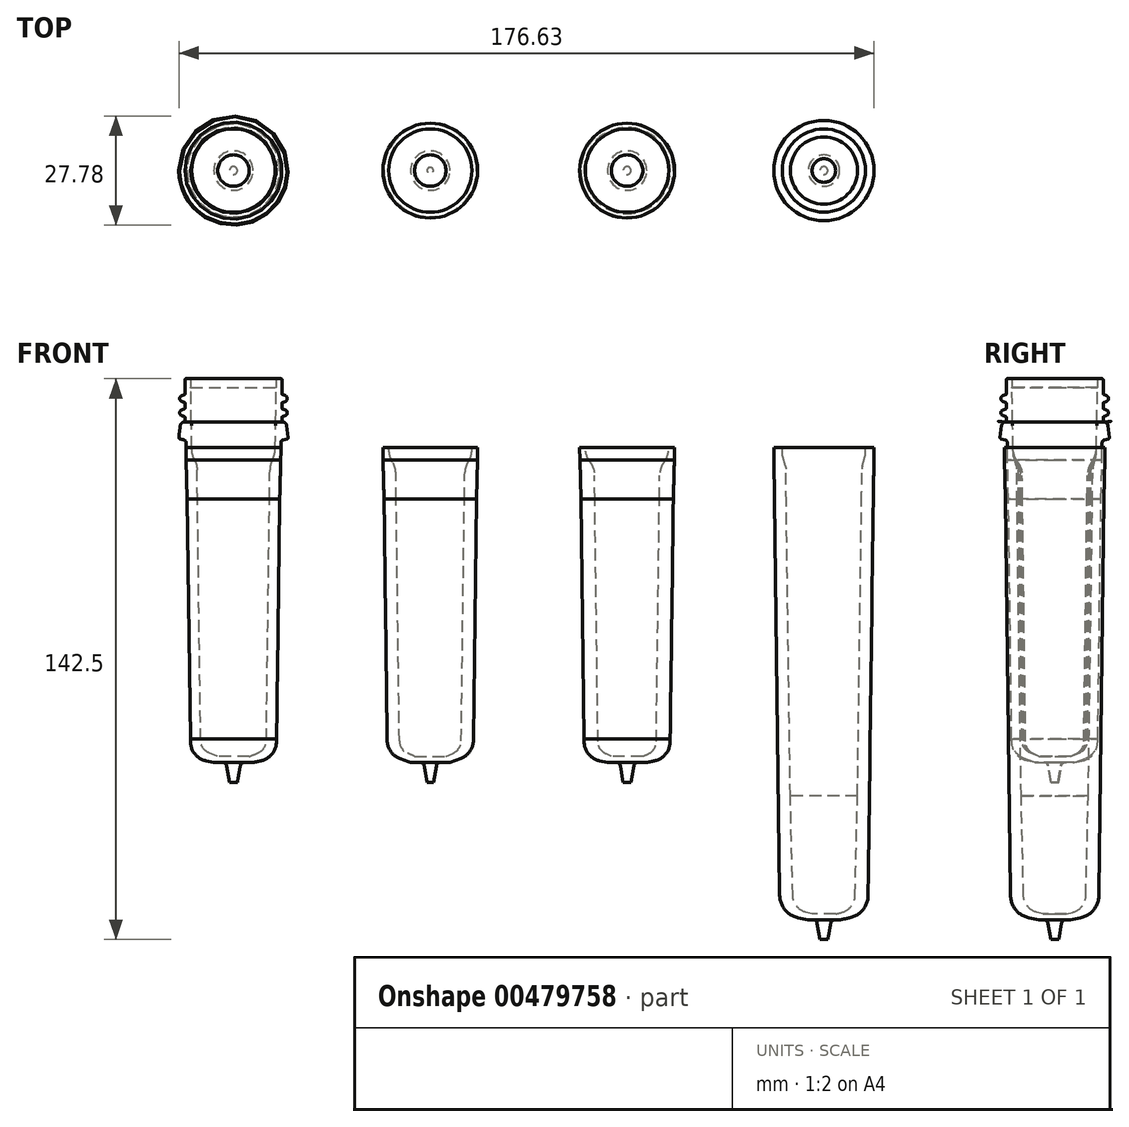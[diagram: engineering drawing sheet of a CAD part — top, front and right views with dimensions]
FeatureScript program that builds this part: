
annotation { "Feature Type Name" : "Feature", "Feature Type Description" : "" }
export const myFeature = defineFeature(function(context is Context, id is Id, definition is map)
    precondition{}
    {
        {
            var Q0;
            Q0=qCreatedBy(makeId("Front.planeOp"),FACE);
            var sketch = newSketch(context, id + "F0", { "sketchPlane" : qUnion([Q0])});
            skLineSegment(sketch, "E0", {"start": v(70.2, -70.1) * mm, "end": v(67.2, -70.1) * mm});
            skLineSegment(sketch, "E1", {"start": v(70.2, -70.1) * mm, "end": v(73.2, -70.1) * mm});
            skLineSegment(sketch, "E2", {"start": v(81.03, 63.6) * mm, "end": v(80.73, 46.79) * mm});
            skLineSegment(sketch, "E3", {"start": v(80.62, 46.02) * mm, "end": v(79.98, 43.78) * mm});
            skLineSegment(sketch, "E4", {"start": v(58.17, 65.9) * mm, "end": v(58.97, 65.9) * mm});
            skLineSegment(sketch, "E5", {"start": v(59.37, 65.5) * mm, "end": v(59.37, 63.6) * mm});
            skLineSegment(sketch, "E6", {"start": v(81.03, 65.5) * mm, "end": v(81.03, 63.6) * mm});
            skArc(sketch, "E7", {"start": v(59.37, 65.5) * mm, "mid": v(59.25, 65.78) * mm, "end": v(58.97, 65.9) * mm});
            skArc(sketch, "E8", {"start": v(81.43, 65.9) * mm, "mid": v(81.15, 65.78) * mm, "end": v(81.03, 65.5) * mm});
            skLineSegment(sketch, "E9", {"start": v(79.87, 43) * mm, "end": v(79.77, 34.4) * mm});
            skLineSegment(sketch, "E10", {"start": v(59.37, 63.6) * mm, "end": v(59.67, 46.79) * mm});
            skLineSegment(sketch, "E11", {"start": v(59.78, 46.02) * mm, "end": v(60.42, 43.78) * mm});
            skLineSegment(sketch, "E12", {"start": v(60.54, 43) * mm, "end": v(60.64, 34.4) * mm});
            skLineSegment(sketch, "E13", {"start": v(78.73, -40.1) * mm, "end": v(79.77, 34.4) * mm});
            skLineSegment(sketch, "E14", {"start": v(61.67, -40.1) * mm, "end": v(60.64, 34.4) * mm});
            skLineSegment(sketch, "E15", {"start": v(73.2, -70.1) * mm, "end": v(74.78, -69.68) * mm});
            skArc(sketch, "E16", {"start": v(74.78, -69.68) * mm, "mid": v(77.15, -68.12) * mm, "end": v(78.1, -65.44) * mm});
            skLineSegment(sketch, "E17", {"start": v(78.1, -65.44) * mm, "end": v(78.73, -40.1) * mm});
            skLineSegment(sketch, "E18", {"start": v(67.2, -70.1) * mm, "end": v(65.63, -69.68) * mm});
            skArc(sketch, "E19", {"start": v(62.3, -65.44) * mm, "mid": v(63.25, -68.12) * mm, "end": v(65.63, -69.68) * mm});
            skLineSegment(sketch, "E20", {"start": v(62.3, -65.44) * mm, "end": v(61.67, -40.1) * mm});
            skLineSegment(sketch, "E21", {"start": v(82.49, 60.98) * mm, "end": v(82.49, 65.65) * mm});
            skArc(sketch, "E22", {"start": v(57.07, 62.5) * mm, "mid": v(56.56, 61.78) * mm, "end": v(57.07, 61.05) * mm});
            skLineSegment(sketch, "E23", {"start": v(56.31, 51.1) * mm, "end": v(56.68, 54.02) * mm});
            skArc(sketch, "E24", {"start": v(56.31, 51.1) * mm, "mid": v(56.37, 50.86) * mm, "end": v(56.58, 50.72) * mm});
            skLineSegment(sketch, "E25", {"start": v(58.32, 49.75) * mm, "end": v(58.32, 48.4) * mm});
            skLineSegment(sketch, "E26", {"start": v(57.79, 50.43) * mm, "end": v(56.58, 50.72) * mm});
            skArc(sketch, "E27", {"start": v(58.32, 49.75) * mm, "mid": v(58.17, 50.18) * mm, "end": v(57.79, 50.43) * mm});
            skLineSegment(sketch, "E28", {"start": v(57.92, 55.1) * mm, "end": v(57.92, 57.14) * mm});
            skArc(sketch, "E29", {"start": v(57.72, 54.9) * mm, "mid": v(57.86, 54.96) * mm, "end": v(57.92, 55.1) * mm});
            skLineSegment(sketch, "E30", {"start": v(57.72, 54.9) * mm, "end": v(57.58, 54.9) * mm});
            skArc(sketch, "E31", {"start": v(57.58, 54.9) * mm, "mid": v(56.98, 54.62) * mm, "end": v(56.68, 54.02) * mm});
            skLineSegment(sketch, "E32", {"start": v(57.92, 60.74) * mm, "end": v(57.07, 61.05) * mm});
            skLineSegment(sketch, "E33", {"start": v(57.92, 57.14) * mm, "end": v(57.07, 57.45) * mm});
            skArc(sketch, "E34", {"start": v(57.07, 58.9) * mm, "mid": v(56.56, 58.18) * mm, "end": v(57.07, 57.45) * mm});
            skLineSegment(sketch, "E35", {"start": v(57.92, 59.2) * mm, "end": v(57.07, 58.9) * mm});
            skLineSegment(sketch, "E36", {"start": v(57.92, 59.2) * mm, "end": v(57.92, 60.74) * mm});
            skLineSegment(sketch, "E37", {"start": v(84.09, 51.1) * mm, "end": v(83.72, 54.02) * mm});
            skLineSegment(sketch, "E38", {"start": v(82.62, 50.43) * mm, "end": v(83.83, 50.72) * mm});
            skArc(sketch, "E39", {"start": v(83.83, 50.72) * mm, "mid": v(84.03, 50.86) * mm, "end": v(84.09, 51.1) * mm});
            skLineSegment(sketch, "E40", {"start": v(82.09, 49.75) * mm, "end": v(82.09, 48.4) * mm});
            skArc(sketch, "E41", {"start": v(82.62, 50.43) * mm, "mid": v(82.23, 50.18) * mm, "end": v(82.09, 49.75) * mm});
            skArc(sketch, "E42", {"start": v(83.33, 55.63) * mm, "mid": v(83.84, 56.35) * mm, "end": v(83.33, 57.08) * mm});
            skArc(sketch, "E43", {"start": v(83.72, 54.02) * mm, "mid": v(83.42, 54.62) * mm, "end": v(82.82, 54.9) * mm});
            skLineSegment(sketch, "E44", {"start": v(82.69, 54.9) * mm, "end": v(82.82, 54.9) * mm});
            skArc(sketch, "E45", {"start": v(82.49, 55.1) * mm, "mid": v(82.54, 54.96) * mm, "end": v(82.69, 54.9) * mm});
            skLineSegment(sketch, "E46", {"start": v(82.49, 55.1) * mm, "end": v(82.49, 55.32) * mm});
            skLineSegment(sketch, "E47", {"start": v(82.49, 55.32) * mm, "end": v(83.33, 55.63) * mm});
            skLineSegment(sketch, "E48", {"start": v(82.49, 60.98) * mm, "end": v(83.33, 60.68) * mm});
            skLineSegment(sketch, "E49", {"start": v(82.49, 57.38) * mm, "end": v(82.49, 58.92) * mm});
            skLineSegment(sketch, "E50", {"start": v(82.49, 57.38) * mm, "end": v(83.33, 57.08) * mm});
            skLineSegment(sketch, "E51", {"start": v(82.49, 58.92) * mm, "end": v(83.33, 59.23) * mm});
            skArc(sketch, "E52", {"start": v(83.33, 59.23) * mm, "mid": v(83.84, 59.95) * mm, "end": v(83.33, 60.68) * mm});
            skLineSegment(sketch, "E53", {"start": v(57.92, 62.8) * mm, "end": v(57.92, 65.65) * mm});
            skLineSegment(sketch, "E54", {"start": v(57.92, 62.8) * mm, "end": v(57.07, 62.5) * mm});
            skLineSegment(sketch, "E55", {"start": v(82.95, 48.4) * mm, "end": v(82.93, 45.4) * mm});
            skLineSegment(sketch, "E56", {"start": v(82.93, 45.4) * mm, "end": v(82.75, 35.4) * mm});
            skLineSegment(sketch, "E57", {"start": v(82.75, 35.4) * mm, "end": v(81.44, -64.6) * mm});
            skLineSegment(sketch, "E58", {"start": v(57.45, 48.4) * mm, "end": v(57.48, 45.4) * mm});
            skLineSegment(sketch, "E59", {"start": v(57.48, 45.4) * mm, "end": v(57.65, 35.4) * mm});
            skLineSegment(sketch, "E60", {"start": v(57.65, 35.4) * mm, "end": v(58.96, -64.6) * mm});
            skLineSegment(sketch, "E61", {"start": v(69.2, -76.6) * mm, "end": v(68.47, -72.43) * mm});
            skLineSegment(sketch, "E62", {"start": v(66.2, -71.6) * mm, "end": v(63.57, -71.04) * mm});
            skLineSegment(sketch, "E63", {"start": v(71.2, -76.6) * mm, "end": v(71.94, -72.43) * mm});
            skLineSegment(sketch, "E64", {"start": v(74.2, -71.6) * mm, "end": v(76.76, -71.06) * mm});
            skArc(sketch, "E65", {"start": v(76.76, -71.06) * mm, "mid": v(80.1, -69.03) * mm, "end": v(81.43, -65.37) * mm});
            skArc(sketch, "E66", {"start": v(72.92, -71.6) * mm, "mid": v(72.28, -71.84) * mm, "end": v(71.94, -72.43) * mm});
            skArc(sketch, "E67", {"start": v(68.47, -72.43) * mm, "mid": v(68.12, -71.84) * mm, "end": v(67.48, -71.6) * mm});
            skLineSegment(sketch, "E68", {"start": v(81.44, -64.6) * mm, "end": v(81.43, -65.37) * mm});
            skArc(sketch, "E69", {"start": v(58.97, -65.37) * mm, "mid": v(60.3, -69.03) * mm, "end": v(63.64, -71.06) * mm});
            skLineSegment(sketch, "E70", {"start": v(58.96, -64.6) * mm, "end": v(58.97, -65.37) * mm});
            skLineSegment(sketch, "E71", {"start": v(71.2, -76.6) * mm, "end": v(69.2, -76.6) * mm});
            skArc(sketch, "E72", {"start": v(59.67, 46.79) * mm, "mid": v(59.7, 46.4) * mm, "end": v(59.78, 46.02) * mm});
            skArc(sketch, "E73", {"start": v(60.54, 43) * mm, "mid": v(60.5, 43.4) * mm, "end": v(60.42, 43.78) * mm});
            skArc(sketch, "E74", {"start": v(80.62, 46.02) * mm, "mid": v(80.7, 46.4) * mm, "end": v(80.73, 46.79) * mm});
            skArc(sketch, "E75", {"start": v(79.98, 43.78) * mm, "mid": v(79.9, 43.4) * mm, "end": v(79.87, 43) * mm});
            skLineSegment(sketch, "E76", {"start": v(58.32, 48.4) * mm, "end": v(57.45, 48.4) * mm});
            skArc(sketch, "E77", {"start": v(58.17, 65.9) * mm, "mid": v(57.99, 65.82) * mm, "end": v(57.92, 65.65) * mm});
            skLineSegment(sketch, "E78", {"start": v(81.43, 65.9) * mm, "end": v(82.24, 65.9) * mm});
            skArc(sketch, "E79", {"start": v(82.49, 65.65) * mm, "mid": v(82.41, 65.82) * mm, "end": v(82.24, 65.9) * mm});
            skLineSegment(sketch, "E80", {"start": v(82.09, 48.4) * mm, "end": v(82.95, 48.4) * mm});
            skLineSegment(sketch, "E81", {"start": v(66.2, -71.6) * mm, "end": v(67.48, -71.6) * mm});
            skLineSegment(sketch, "E82", {"start": v(72.92, -71.6) * mm, "end": v(74.2, -71.6) * mm});
            skLineSegment(sketch, "E83", {"start": v(33.7, 54.02) * mm, "end": v(34.08, 51) * mm});
            skArc(sketch, "E84", {"start": v(33.82, 50.62) * mm, "mid": v(34.02, 50.76) * mm, "end": v(34.08, 51) * mm});
            skArc(sketch, "E85", {"start": v(32.78, 50.36) * mm, "mid": v(32.4, 50.12) * mm, "end": v(32.25, 49.68) * mm});
            skLineSegment(sketch, "E86", {"start": v(32.25, 48.4) * mm, "end": v(32.25, 49.68) * mm});
            skLineSegment(sketch, "E87", {"start": v(32.78, 50.36) * mm, "end": v(33.82, 50.62) * mm});
            skArc(sketch, "E88", {"start": v(33.36, 61.94) * mm, "mid": v(33.87, 62.66) * mm, "end": v(33.36, 63.39) * mm});
            skLineSegment(sketch, "E89", {"start": v(33.3, 54.71) * mm, "end": v(33.36, 54.74) * mm});
            skArc(sketch, "E90", {"start": v(33.7, 54.02) * mm, "mid": v(33.57, 54.41) * mm, "end": v(33.3, 54.71) * mm});
            skArc(sketch, "E91", {"start": v(33.36, 54.74) * mm, "mid": v(33.87, 55.46) * mm, "end": v(33.36, 56.19) * mm});
            skArc(sketch, "E92", {"start": v(33.36, 58.34) * mm, "mid": v(33.87, 59.06) * mm, "end": v(33.36, 59.79) * mm});
            skLineSegment(sketch, "E93", {"start": v(32.51, 57.89) * mm, "end": v(32.51, 56.64) * mm});
            skArc(sketch, "E94", {"start": v(32.51, 56.64) * mm, "mid": v(32.55, 56.52) * mm, "end": v(32.64, 56.45) * mm});
            skArc(sketch, "E95", {"start": v(32.64, 58.08) * mm, "mid": v(32.55, 58) * mm, "end": v(32.51, 57.89) * mm});
            skArc(sketch, "E96", {"start": v(32.51, 60.24) * mm, "mid": v(32.55, 60.12) * mm, "end": v(32.64, 60.05) * mm});
            skArc(sketch, "E97", {"start": v(32.64, 61.68) * mm, "mid": v(32.55, 61.6) * mm, "end": v(32.51, 61.49) * mm});
            skLineSegment(sketch, "E98", {"start": v(32.51, 61.49) * mm, "end": v(32.51, 60.24) * mm});
            skArc(sketch, "E99", {"start": v(32.51, 63.84) * mm, "mid": v(32.55, 63.72) * mm, "end": v(32.64, 63.65) * mm});
            skLineSegment(sketch, "E100", {"start": v(32.51, 65.65) * mm, "end": v(32.51, 63.84) * mm});
            skLineSegment(sketch, "E101", {"start": v(32.64, 56.45) * mm, "end": v(33.36, 56.19) * mm});
            skLineSegment(sketch, "E102", {"start": v(32.64, 58.08) * mm, "end": v(33.36, 58.34) * mm});
            skLineSegment(sketch, "E103", {"start": v(32.64, 60.05) * mm, "end": v(33.36, 59.79) * mm});
            skLineSegment(sketch, "E104", {"start": v(32.64, 61.68) * mm, "end": v(33.36, 61.94) * mm});
            skLineSegment(sketch, "E105", {"start": v(32.64, 63.65) * mm, "end": v(33.36, 63.39) * mm});
            skLineSegment(sketch, "E106", {"start": v(7.9, 65.65) * mm, "end": v(7.9, 62.9) * mm});
            skLineSegment(sketch, "E107", {"start": v(7.9, 62.9) * mm, "end": v(7.9, 62.04) * mm});
            skLineSegment(sketch, "E108", {"start": v(7.76, 61.85) * mm, "end": v(7.04, 61.59) * mm});
            skLineSegment(sketch, "E109", {"start": v(7.76, 59.88) * mm, "end": v(7.04, 60.14) * mm});
            skArc(sketch, "E110", {"start": v(7.04, 61.59) * mm, "mid": v(6.53, 60.86) * mm, "end": v(7.04, 60.14) * mm});
            skArc(sketch, "E111", {"start": v(7.76, 61.85) * mm, "mid": v(7.86, 61.92) * mm, "end": v(7.9, 62.04) * mm});
            skArc(sketch, "E112", {"start": v(7.9, 59.69) * mm, "mid": v(7.86, 59.8) * mm, "end": v(7.76, 59.88) * mm});
            skLineSegment(sketch, "E113", {"start": v(7.76, 58.25) * mm, "end": v(7.04, 57.99) * mm});
            skArc(sketch, "E114", {"start": v(7.76, 58.25) * mm, "mid": v(7.86, 58.32) * mm, "end": v(7.9, 58.44) * mm});
            skLineSegment(sketch, "E115", {"start": v(7.9, 59.69) * mm, "end": v(7.9, 58.44) * mm});
            skLineSegment(sketch, "E116", {"start": v(7.62, 50.36) * mm, "end": v(6.58, 50.62) * mm});
            skLineSegment(sketch, "E117", {"start": v(6.7, 54.02) * mm, "end": v(6.32, 51) * mm});
            skLineSegment(sketch, "E118", {"start": v(8.15, 48.4) * mm, "end": v(8.15, 49.68) * mm});
            skArc(sketch, "E119", {"start": v(8.15, 49.68) * mm, "mid": v(8, 50.12) * mm, "end": v(7.62, 50.36) * mm});
            skArc(sketch, "E120", {"start": v(6.32, 51) * mm, "mid": v(6.38, 50.76) * mm, "end": v(6.58, 50.62) * mm});
            skArc(sketch, "E121", {"start": v(7.7, 54.9) * mm, "mid": v(7.03, 54.65) * mm, "end": v(6.7, 54.02) * mm});
            skArc(sketch, "E122", {"start": v(7.7, 54.9) * mm, "mid": v(7.83, 54.95) * mm, "end": v(7.9, 55.1) * mm});
            skLineSegment(sketch, "E123", {"start": v(7.76, 56.28) * mm, "end": v(7.04, 56.54) * mm});
            skArc(sketch, "E124", {"start": v(7.04, 57.99) * mm, "mid": v(6.53, 57.26) * mm, "end": v(7.04, 56.54) * mm});
            skArc(sketch, "E125", {"start": v(7.9, 56.09) * mm, "mid": v(7.86, 56.2) * mm, "end": v(7.76, 56.28) * mm});
            skLineSegment(sketch, "E126", {"start": v(7.9, 56.09) * mm, "end": v(7.9, 55.1) * mm});
            skLineSegment(sketch, "E127", {"start": v(8.15, 48.4) * mm, "end": v(8.2, 45.3) * mm});
            skLineSegment(sketch, "E128", {"start": v(8.2, 45.3) * mm, "end": v(8.45, 35.3) * mm});
            skLineSegment(sketch, "E129", {"start": v(32.25, 48.4) * mm, "end": v(32.21, 45.3) * mm});
            skLineSegment(sketch, "E130", {"start": v(32.21, 45.3) * mm, "end": v(31.95, 35.3) * mm});
            skLineSegment(sketch, "E131", {"start": v(31.95, 35.3) * mm, "end": v(31.15, -25.6) * mm});
            skLineSegment(sketch, "E132", {"start": v(8.45, 35.3) * mm, "end": v(9.25, -25.6) * mm});
            skLineSegment(sketch, "E133", {"start": v(21.2, -36.6) * mm, "end": v(21.94, -32.43) * mm});
            skLineSegment(sketch, "E134", {"start": v(19.2, -36.6) * mm, "end": v(18.47, -32.43) * mm});
            skLineSegment(sketch, "E135", {"start": v(9.28, -25.6) * mm, "end": v(9.29, -26.36) * mm});
            skLineSegment(sketch, "E136", {"start": v(15.2, -31.6) * mm, "end": v(13.25, -31.19) * mm});
            skArc(sketch, "E137", {"start": v(9.29, -26.36) * mm, "mid": v(10.42, -29.47) * mm, "end": v(13.25, -31.19) * mm});
            skLineSegment(sketch, "E138", {"start": v(15.2, -31.6) * mm, "end": v(17.48, -31.6) * mm});
            skArc(sketch, "E139", {"start": v(18.47, -32.43) * mm, "mid": v(18.12, -31.84) * mm, "end": v(17.48, -31.6) * mm});
            skArc(sketch, "E140", {"start": v(22.92, -31.6) * mm, "mid": v(22.28, -31.84) * mm, "end": v(21.94, -32.43) * mm});
            skLineSegment(sketch, "E141", {"start": v(31.13, -25.6) * mm, "end": v(31.12, -26.36) * mm});
            skArc(sketch, "E142", {"start": v(27.16, -31.19) * mm, "mid": v(29.98, -29.47) * mm, "end": v(31.12, -26.36) * mm});
            skLineSegment(sketch, "E143", {"start": v(25.2, -31.6) * mm, "end": v(22.92, -31.6) * mm});
            skLineSegment(sketch, "E144", {"start": v(25.2, -31.6) * mm, "end": v(27.16, -31.19) * mm});
            skArc(sketch, "E145", {"start": v(12.8, -26.29) * mm, "mid": v(13.4, -28.2) * mm, "end": v(14.93, -29.46) * mm});
            skLineSegment(sketch, "E146", {"start": v(12, 35.3) * mm, "end": v(12.8, -26.29) * mm});
            skArc(sketch, "E147", {"start": v(9.35, 65.6) * mm, "mid": v(9.26, 65.8) * mm, "end": v(9.05, 65.9) * mm});
            skLineSegment(sketch, "E148", {"start": v(9.05, 65.9) * mm, "end": v(8.14, 65.9) * mm});
            skLineSegment(sketch, "E149", {"start": v(9.35, 65.6) * mm, "end": v(9.35, 63.62) * mm});
            skLineSegment(sketch, "E150", {"start": v(9.35, 63.6) * mm, "end": v(9.61, 48.24) * mm});
            skLineSegment(sketch, "E151", {"start": v(11.92, 41.34) * mm, "end": v(12, 35.3) * mm});
            skArc(sketch, "E152", {"start": v(25.47, -29.46) * mm, "mid": v(27.01, -28.2) * mm, "end": v(27.6, -26.29) * mm});
            skLineSegment(sketch, "E153", {"start": v(24.2, -30) * mm, "end": v(25.47, -29.46) * mm});
            skLineSegment(sketch, "E154", {"start": v(16.2, -30) * mm, "end": v(14.93, -29.46) * mm});
            skLineSegment(sketch, "E155", {"start": v(28.41, 35.3) * mm, "end": v(27.6, -26.29) * mm});
            skArc(sketch, "E156", {"start": v(31.36, 65.9) * mm, "mid": v(31.14, 65.8) * mm, "end": v(31.06, 65.6) * mm});
            skLineSegment(sketch, "E157", {"start": v(31.06, 65.6) * mm, "end": v(31.06, 63.6) * mm});
            skLineSegment(sketch, "E158", {"start": v(32.26, 65.9) * mm, "end": v(31.36, 65.9) * mm});
            skLineSegment(sketch, "E159", {"start": v(31.06, 63.6) * mm, "end": v(30.79, 48.24) * mm});
            skLineSegment(sketch, "E160", {"start": v(28.48, 41.34) * mm, "end": v(28.41, 35.3) * mm});
            skLineSegment(sketch, "E161", {"start": v(16.2, -30) * mm, "end": v(20.2, -30) * mm});
            skLineSegment(sketch, "E162", {"start": v(24.2, -30) * mm, "end": v(20.2, -30) * mm});
            skArc(sketch, "E163", {"start": v(11.92, 41.34) * mm, "mid": v(11.61, 43.16) * mm, "end": v(10.77, 44.8) * mm});
            skArc(sketch, "E164", {"start": v(9.61, 48.24) * mm, "mid": v(9.93, 46.43) * mm, "end": v(10.77, 44.8) * mm});
            skArc(sketch, "E165", {"start": v(29.64, 44.8) * mm, "mid": v(28.79, 43.16) * mm, "end": v(28.48, 41.34) * mm});
            skArc(sketch, "E166", {"start": v(29.64, 44.8) * mm, "mid": v(30.48, 46.43) * mm, "end": v(30.79, 48.24) * mm});
            skLineSegment(sketch, "E167", {"start": v(19.2, -36.6) * mm, "end": v(21.2, -36.6) * mm});
            skArc(sketch, "E168", {"start": v(8.14, 65.9) * mm, "mid": v(7.96, 65.82) * mm, "end": v(7.9, 65.65) * mm});
            skArc(sketch, "E169", {"start": v(32.51, 65.65) * mm, "mid": v(32.44, 65.82) * mm, "end": v(32.26, 65.9) * mm});
            skLineSegment(sketch, "E170", {"start": v(-41.85, 48.4) * mm, "end": v(-41.8, 45.3) * mm});
            skLineSegment(sketch, "E171", {"start": v(-41.8, 45.3) * mm, "end": v(-41.55, 35.3) * mm});
            skLineSegment(sketch, "E172", {"start": v(-17.75, 48.4) * mm, "end": v(-17.79, 45.3) * mm});
            skLineSegment(sketch, "E173", {"start": v(-17.79, 45.3) * mm, "end": v(-18.05, 35.3) * mm});
            skLineSegment(sketch, "E174", {"start": v(-18.05, 35.3) * mm, "end": v(-18.85, -25.6) * mm});
            skLineSegment(sketch, "E175", {"start": v(-41.55, 35.3) * mm, "end": v(-40.75, -25.6) * mm});
            skArc(sketch, "E176", {"start": v(-27.28, -31.6) * mm, "mid": v(-27.92, -31.84) * mm, "end": v(-28.26, -32.43) * mm});
            skLineSegment(sketch, "E177", {"start": v(-29, -36.6) * mm, "end": v(-28.26, -32.43) * mm});
            skLineSegment(sketch, "E178", {"start": v(-29, -36.6) * mm, "end": v(-29.8, -36.6) * mm});
            skLineSegment(sketch, "E179", {"start": v(-24.8, -31.6) * mm, "end": v(-21.93, -30.5) * mm});
            skLineSegment(sketch, "E180", {"start": v(-34.8, -31.6) * mm, "end": v(-37.66, -30.5) * mm});
            skLineSegment(sketch, "E181", {"start": v(-30.6, -36.6) * mm, "end": v(-29.8, -36.6) * mm});
            skLineSegment(sketch, "E182", {"start": v(-30.6, -36.6) * mm, "end": v(-31.33, -32.43) * mm});
            skArc(sketch, "E183", {"start": v(-31.33, -32.43) * mm, "mid": v(-31.68, -31.84) * mm, "end": v(-32.32, -31.6) * mm});
            skArc(sketch, "E184", {"start": v(-21.93, -30.5) * mm, "mid": v(-19.72, -28.77) * mm, "end": v(-18.85, -26.09) * mm});
            skArc(sketch, "E185", {"start": v(-40.74, -26.09) * mm, "mid": v(-39.88, -28.77) * mm, "end": v(-37.66, -30.5) * mm});
            skLineSegment(sketch, "E186", {"start": v(-18.85, -25.6) * mm, "end": v(-18.85, -26.09) * mm});
            skLineSegment(sketch, "E187", {"start": v(-40.75, -25.6) * mm, "end": v(-40.74, -26.09) * mm});
            skLineSegment(sketch, "E188", {"start": v(-33.8, -30) * mm, "end": v(-35.52, -29.27) * mm});
            skLineSegment(sketch, "E189", {"start": v(-38.46, 35.3) * mm, "end": v(-37.65, -26.1) * mm});
            skLineSegment(sketch, "E190", {"start": v(-40.65, 63.6) * mm, "end": v(-40.38, 47.9) * mm});
            skLineSegment(sketch, "E191", {"start": v(-40.65, 65.6) * mm, "end": v(-40.65, 63.62) * mm});
            skLineSegment(sketch, "E192", {"start": v(-40.95, 65.9) * mm, "end": v(-41.86, 65.9) * mm});
            skArc(sketch, "E193", {"start": v(-40.65, 65.6) * mm, "mid": v(-40.74, 65.8) * mm, "end": v(-40.95, 65.9) * mm});
            skLineSegment(sketch, "E194", {"start": v(-39.53, 44.92) * mm, "end": v(-39.39, 44.69) * mm});
            skLineSegment(sketch, "E195", {"start": v(-38.53, 41.67) * mm, "end": v(-38.46, 35.3) * mm});
            skArc(sketch, "E196", {"start": v(-37.65, -26.1) * mm, "mid": v(-37.06, -28) * mm, "end": v(-35.52, -29.27) * mm});
            skLineSegment(sketch, "E197", {"start": v(-21.14, 35.3) * mm, "end": v(-21.94, -26.1) * mm});
            skLineSegment(sketch, "E198", {"start": v(-18.94, 63.6) * mm, "end": v(-19.22, 47.9) * mm});
            skLineSegment(sketch, "E199", {"start": v(-18.94, 65.6) * mm, "end": v(-18.94, 63.6) * mm});
            skLineSegment(sketch, "E200", {"start": v(-17.74, 65.9) * mm, "end": v(-18.64, 65.9) * mm});
            skArc(sketch, "E201", {"start": v(-18.64, 65.9) * mm, "mid": v(-18.86, 65.8) * mm, "end": v(-18.94, 65.6) * mm});
            skLineSegment(sketch, "E202", {"start": v(-20.07, 44.92) * mm, "end": v(-20.2, 44.69) * mm});
            skLineSegment(sketch, "E203", {"start": v(-21.06, 41.67) * mm, "end": v(-21.14, 35.3) * mm});
            skLineSegment(sketch, "E204", {"start": v(-33.8, -30) * mm, "end": v(-29.8, -30) * mm});
            skLineSegment(sketch, "E205", {"start": v(-25.8, -30) * mm, "end": v(-24.08, -29.27) * mm});
            skArc(sketch, "E206", {"start": v(-24.08, -29.27) * mm, "mid": v(-22.54, -28) * mm, "end": v(-21.94, -26.1) * mm});
            skLineSegment(sketch, "E207", {"start": v(-25.8, -30) * mm, "end": v(-29.8, -30) * mm});
            skLineSegment(sketch, "E208", {"start": v(-16.3, 54.02) * mm, "end": v(-15.92, 51) * mm});
            skArc(sketch, "E209", {"start": v(-16.18, 50.62) * mm, "mid": v(-15.98, 50.76) * mm, "end": v(-15.92, 51) * mm});
            skArc(sketch, "E210", {"start": v(-17.22, 50.36) * mm, "mid": v(-17.6, 50.12) * mm, "end": v(-17.75, 49.68) * mm});
            skLineSegment(sketch, "E211", {"start": v(-17.75, 48.4) * mm, "end": v(-17.75, 49.68) * mm});
            skLineSegment(sketch, "E212", {"start": v(-17.22, 50.36) * mm, "end": v(-16.18, 50.62) * mm});
            skArc(sketch, "E213", {"start": v(-16.64, 61.94) * mm, "mid": v(-16.13, 62.66) * mm, "end": v(-16.64, 63.39) * mm});
            skLineSegment(sketch, "E214", {"start": v(-16.7, 54.71) * mm, "end": v(-16.64, 54.74) * mm});
            skArc(sketch, "E215", {"start": v(-16.3, 54.02) * mm, "mid": v(-16.43, 54.41) * mm, "end": v(-16.7, 54.71) * mm});
            skArc(sketch, "E216", {"start": v(-16.64, 54.74) * mm, "mid": v(-16.13, 55.46) * mm, "end": v(-16.64, 56.19) * mm});
            skArc(sketch, "E217", {"start": v(-16.64, 58.34) * mm, "mid": v(-16.13, 59.06) * mm, "end": v(-16.64, 59.79) * mm});
            skLineSegment(sketch, "E218", {"start": v(-17.49, 57.89) * mm, "end": v(-17.49, 56.64) * mm});
            skArc(sketch, "E219", {"start": v(-17.49, 56.64) * mm, "mid": v(-17.45, 56.52) * mm, "end": v(-17.36, 56.45) * mm});
            skArc(sketch, "E220", {"start": v(-17.36, 58.08) * mm, "mid": v(-17.45, 58) * mm, "end": v(-17.49, 57.89) * mm});
            skArc(sketch, "E221", {"start": v(-17.49, 60.24) * mm, "mid": v(-17.45, 60.12) * mm, "end": v(-17.36, 60.05) * mm});
            skArc(sketch, "E222", {"start": v(-17.36, 61.68) * mm, "mid": v(-17.45, 61.6) * mm, "end": v(-17.49, 61.49) * mm});
            skLineSegment(sketch, "E223", {"start": v(-17.49, 61.49) * mm, "end": v(-17.49, 60.24) * mm});
            skArc(sketch, "E224", {"start": v(-17.49, 63.84) * mm, "mid": v(-17.45, 63.72) * mm, "end": v(-17.36, 63.65) * mm});
            skLineSegment(sketch, "E225", {"start": v(-17.49, 65.65) * mm, "end": v(-17.49, 63.84) * mm});
            skLineSegment(sketch, "E226", {"start": v(-17.36, 56.45) * mm, "end": v(-16.64, 56.19) * mm});
            skLineSegment(sketch, "E227", {"start": v(-17.36, 58.08) * mm, "end": v(-16.64, 58.34) * mm});
            skLineSegment(sketch, "E228", {"start": v(-17.36, 60.05) * mm, "end": v(-16.64, 59.79) * mm});
            skLineSegment(sketch, "E229", {"start": v(-17.36, 61.68) * mm, "end": v(-16.64, 61.94) * mm});
            skLineSegment(sketch, "E230", {"start": v(-17.36, 63.65) * mm, "end": v(-16.64, 63.39) * mm});
            skLineSegment(sketch, "E231", {"start": v(-42.1, 65.65) * mm, "end": v(-42.1, 62.9) * mm});
            skLineSegment(sketch, "E232", {"start": v(-42.1, 62.9) * mm, "end": v(-42.1, 62.04) * mm});
            skLineSegment(sketch, "E233", {"start": v(-42.24, 61.85) * mm, "end": v(-42.96, 61.59) * mm});
            skLineSegment(sketch, "E234", {"start": v(-42.24, 59.88) * mm, "end": v(-42.96, 60.14) * mm});
            skArc(sketch, "E235", {"start": v(-42.96, 61.59) * mm, "mid": v(-43.47, 60.86) * mm, "end": v(-42.96, 60.14) * mm});
            skArc(sketch, "E236", {"start": v(-42.24, 61.85) * mm, "mid": v(-42.14, 61.92) * mm, "end": v(-42.1, 62.04) * mm});
            skArc(sketch, "E237", {"start": v(-42.1, 59.69) * mm, "mid": v(-42.14, 59.8) * mm, "end": v(-42.24, 59.88) * mm});
            skLineSegment(sketch, "E238", {"start": v(-42.24, 58.25) * mm, "end": v(-42.96, 57.99) * mm});
            skArc(sketch, "E239", {"start": v(-42.24, 58.25) * mm, "mid": v(-42.14, 58.32) * mm, "end": v(-42.1, 58.44) * mm});
            skLineSegment(sketch, "E240", {"start": v(-42.1, 59.69) * mm, "end": v(-42.1, 58.44) * mm});
            skLineSegment(sketch, "E241", {"start": v(-42.38, 50.36) * mm, "end": v(-43.42, 50.62) * mm});
            skLineSegment(sketch, "E242", {"start": v(-43.3, 54.02) * mm, "end": v(-43.68, 51) * mm});
            skLineSegment(sketch, "E243", {"start": v(-41.85, 48.4) * mm, "end": v(-41.85, 49.68) * mm});
            skArc(sketch, "E244", {"start": v(-41.85, 49.68) * mm, "mid": v(-42, 50.12) * mm, "end": v(-42.38, 50.36) * mm});
            skArc(sketch, "E245", {"start": v(-43.68, 51) * mm, "mid": v(-43.62, 50.76) * mm, "end": v(-43.42, 50.62) * mm});
            skArc(sketch, "E246", {"start": v(-42.3, 54.9) * mm, "mid": v(-42.97, 54.65) * mm, "end": v(-43.3, 54.02) * mm});
            skArc(sketch, "E247", {"start": v(-42.3, 54.9) * mm, "mid": v(-42.17, 54.95) * mm, "end": v(-42.1, 55.1) * mm});
            skLineSegment(sketch, "E248", {"start": v(-42.24, 56.28) * mm, "end": v(-42.96, 56.54) * mm});
            skArc(sketch, "E249", {"start": v(-42.96, 57.99) * mm, "mid": v(-43.47, 57.26) * mm, "end": v(-42.96, 56.54) * mm});
            skArc(sketch, "E250", {"start": v(-42.1, 56.09) * mm, "mid": v(-42.14, 56.2) * mm, "end": v(-42.24, 56.28) * mm});
            skLineSegment(sketch, "E251", {"start": v(-42.1, 56.09) * mm, "end": v(-42.1, 55.1) * mm});
            skLineSegment(sketch, "E252", {"start": v(-34.8, -31.6) * mm, "end": v(-32.32, -31.6) * mm});
            skLineSegment(sketch, "E253", {"start": v(-27.28, -31.6) * mm, "end": v(-24.8, -31.6) * mm});
            skArc(sketch, "E254", {"start": v(-40.38, 47.9) * mm, "mid": v(-40.15, 46.35) * mm, "end": v(-39.53, 44.92) * mm});
            skArc(sketch, "E255", {"start": v(-38.53, 41.67) * mm, "mid": v(-38.76, 43.24) * mm, "end": v(-39.39, 44.69) * mm});
            skArc(sketch, "E256", {"start": v(-20.07, 44.92) * mm, "mid": v(-19.45, 46.35) * mm, "end": v(-19.22, 47.9) * mm});
            skArc(sketch, "E257", {"start": v(-20.2, 44.69) * mm, "mid": v(-20.84, 43.24) * mm, "end": v(-21.06, 41.67) * mm});
            skArc(sketch, "E258", {"start": v(-17.49, 65.65) * mm, "mid": v(-17.56, 65.82) * mm, "end": v(-17.74, 65.9) * mm});
            skArc(sketch, "E259", {"start": v(-41.86, 65.9) * mm, "mid": v(-42.04, 65.82) * mm, "end": v(-42.1, 65.65) * mm});
            skLineSegment(sketch, "E260", {"start": v(-66.3, 54.02) * mm, "end": v(-65.92, 51) * mm});
            skArc(sketch, "E261", {"start": v(-66.18, 50.62) * mm, "mid": v(-65.98, 50.76) * mm, "end": v(-65.92, 51) * mm});
            skArc(sketch, "E262", {"start": v(-67.22, 50.36) * mm, "mid": v(-67.6, 50.12) * mm, "end": v(-67.75, 49.68) * mm});
            skLineSegment(sketch, "E263", {"start": v(-67.75, 48.4) * mm, "end": v(-67.75, 49.68) * mm});
            skLineSegment(sketch, "E264", {"start": v(-67.22, 50.36) * mm, "end": v(-66.18, 50.62) * mm});
            skArc(sketch, "E265", {"start": v(-66.64, 61.94) * mm, "mid": v(-66.13, 62.66) * mm, "end": v(-66.64, 63.39) * mm});
            skLineSegment(sketch, "E266", {"start": v(-66.7, 54.71) * mm, "end": v(-66.64, 54.74) * mm});
            skArc(sketch, "E267", {"start": v(-66.3, 54.02) * mm, "mid": v(-66.43, 54.41) * mm, "end": v(-66.7, 54.71) * mm});
            skArc(sketch, "E268", {"start": v(-66.64, 54.74) * mm, "mid": v(-66.13, 55.46) * mm, "end": v(-66.64, 56.19) * mm});
            skArc(sketch, "E269", {"start": v(-66.64, 58.34) * mm, "mid": v(-66.13, 59.06) * mm, "end": v(-66.64, 59.79) * mm});
            skLineSegment(sketch, "E270", {"start": v(-67.49, 57.89) * mm, "end": v(-67.49, 56.64) * mm});
            skArc(sketch, "E271", {"start": v(-67.49, 56.64) * mm, "mid": v(-67.45, 56.52) * mm, "end": v(-67.36, 56.45) * mm});
            skArc(sketch, "E272", {"start": v(-67.36, 58.08) * mm, "mid": v(-67.45, 58) * mm, "end": v(-67.49, 57.89) * mm});
            skArc(sketch, "E273", {"start": v(-67.49, 60.24) * mm, "mid": v(-67.45, 60.12) * mm, "end": v(-67.36, 60.05) * mm});
            skArc(sketch, "E274", {"start": v(-67.36, 61.68) * mm, "mid": v(-67.45, 61.6) * mm, "end": v(-67.49, 61.49) * mm});
            skLineSegment(sketch, "E275", {"start": v(-67.49, 61.49) * mm, "end": v(-67.49, 60.24) * mm});
            skArc(sketch, "E276", {"start": v(-67.49, 63.84) * mm, "mid": v(-67.45, 63.72) * mm, "end": v(-67.36, 63.65) * mm});
            skLineSegment(sketch, "E277", {"start": v(-67.49, 65.65) * mm, "end": v(-67.49, 63.84) * mm});
            skLineSegment(sketch, "E278", {"start": v(-67.36, 56.45) * mm, "end": v(-66.64, 56.19) * mm});
            skLineSegment(sketch, "E279", {"start": v(-67.36, 58.08) * mm, "end": v(-66.64, 58.34) * mm});
            skLineSegment(sketch, "E280", {"start": v(-67.36, 60.05) * mm, "end": v(-66.64, 59.79) * mm});
            skLineSegment(sketch, "E281", {"start": v(-67.36, 61.68) * mm, "end": v(-66.64, 61.94) * mm});
            skLineSegment(sketch, "E282", {"start": v(-67.36, 63.65) * mm, "end": v(-66.64, 63.39) * mm});
            skLineSegment(sketch, "E283", {"start": v(-92.1, 65.65) * mm, "end": v(-92.1, 62.9) * mm});
            skLineSegment(sketch, "E284", {"start": v(-92.1, 62.9) * mm, "end": v(-92.1, 62.04) * mm});
            skLineSegment(sketch, "E285", {"start": v(-92.24, 61.85) * mm, "end": v(-92.96, 61.59) * mm});
            skLineSegment(sketch, "E286", {"start": v(-92.24, 59.88) * mm, "end": v(-92.96, 60.14) * mm});
            skArc(sketch, "E287", {"start": v(-92.96, 61.59) * mm, "mid": v(-93.47, 60.86) * mm, "end": v(-92.96, 60.14) * mm});
            skArc(sketch, "E288", {"start": v(-92.24, 61.85) * mm, "mid": v(-92.14, 61.92) * mm, "end": v(-92.1, 62.04) * mm});
            skArc(sketch, "E289", {"start": v(-92.1, 59.69) * mm, "mid": v(-92.14, 59.8) * mm, "end": v(-92.24, 59.88) * mm});
            skLineSegment(sketch, "E290", {"start": v(-92.24, 58.25) * mm, "end": v(-92.96, 57.99) * mm});
            skArc(sketch, "E291", {"start": v(-92.24, 58.25) * mm, "mid": v(-92.14, 58.32) * mm, "end": v(-92.1, 58.44) * mm});
            skLineSegment(sketch, "E292", {"start": v(-92.1, 59.69) * mm, "end": v(-92.1, 58.44) * mm});
            skLineSegment(sketch, "E293", {"start": v(-92.38, 50.36) * mm, "end": v(-93.42, 50.62) * mm});
            skLineSegment(sketch, "E294", {"start": v(-93.3, 54.02) * mm, "end": v(-93.68, 51) * mm});
            skLineSegment(sketch, "E295", {"start": v(-91.85, 48.4) * mm, "end": v(-91.85, 49.68) * mm});
            skArc(sketch, "E296", {"start": v(-91.85, 49.68) * mm, "mid": v(-92, 50.12) * mm, "end": v(-92.38, 50.36) * mm});
            skArc(sketch, "E297", {"start": v(-93.68, 51) * mm, "mid": v(-93.62, 50.76) * mm, "end": v(-93.42, 50.62) * mm});
            skArc(sketch, "E298", {"start": v(-92.3, 54.9) * mm, "mid": v(-92.97, 54.65) * mm, "end": v(-93.3, 54.02) * mm});
            skArc(sketch, "E299", {"start": v(-92.3, 54.9) * mm, "mid": v(-92.17, 54.95) * mm, "end": v(-92.1, 55.1) * mm});
            skLineSegment(sketch, "E300", {"start": v(-92.24, 56.28) * mm, "end": v(-92.96, 56.54) * mm});
            skArc(sketch, "E301", {"start": v(-92.96, 57.99) * mm, "mid": v(-93.47, 57.26) * mm, "end": v(-92.96, 56.54) * mm});
            skArc(sketch, "E302", {"start": v(-92.1, 56.09) * mm, "mid": v(-92.14, 56.2) * mm, "end": v(-92.24, 56.28) * mm});
            skLineSegment(sketch, "E303", {"start": v(-92.1, 56.09) * mm, "end": v(-92.1, 55.1) * mm});
            skLineSegment(sketch, "E304", {"start": v(-91.85, 48.4) * mm, "end": v(-91.8, 45.3) * mm});
            skLineSegment(sketch, "E305", {"start": v(-91.8, 45.3) * mm, "end": v(-91.55, 35.3) * mm});
            skLineSegment(sketch, "E306", {"start": v(-67.75, 48.4) * mm, "end": v(-67.79, 45.3) * mm});
            skLineSegment(sketch, "E307", {"start": v(-67.79, 45.3) * mm, "end": v(-68.05, 35.3) * mm});
            skLineSegment(sketch, "E308", {"start": v(-68.05, 35.3) * mm, "end": v(-68.85, -25.6) * mm});
            skLineSegment(sketch, "E309", {"start": v(-91.55, 35.3) * mm, "end": v(-90.75, -25.6) * mm});
            skLineSegment(sketch, "E310", {"start": v(-78.8, -36.6) * mm, "end": v(-78.06, -32.43) * mm});
            skLineSegment(sketch, "E311", {"start": v(-80.8, -36.6) * mm, "end": v(-81.53, -32.43) * mm});
            skLineSegment(sketch, "E312", {"start": v(-90.72, -25.6) * mm, "end": v(-90.71, -26.36) * mm});
            skLineSegment(sketch, "E313", {"start": v(-84.8, -31.6) * mm, "end": v(-86.75, -31.19) * mm});
            skArc(sketch, "E314", {"start": v(-90.71, -26.36) * mm, "mid": v(-89.58, -29.47) * mm, "end": v(-86.75, -31.19) * mm});
            skLineSegment(sketch, "E315", {"start": v(-84.8, -31.6) * mm, "end": v(-82.52, -31.6) * mm});
            skArc(sketch, "E316", {"start": v(-81.53, -32.43) * mm, "mid": v(-81.88, -31.84) * mm, "end": v(-82.52, -31.6) * mm});
            skArc(sketch, "E317", {"start": v(-77.08, -31.6) * mm, "mid": v(-77.72, -31.84) * mm, "end": v(-78.06, -32.43) * mm});
            skLineSegment(sketch, "E318", {"start": v(-68.87, -25.6) * mm, "end": v(-68.88, -26.36) * mm});
            skArc(sketch, "E319", {"start": v(-72.84, -31.19) * mm, "mid": v(-70.02, -29.47) * mm, "end": v(-68.88, -26.36) * mm});
            skLineSegment(sketch, "E320", {"start": v(-74.8, -31.6) * mm, "end": v(-77.08, -31.6) * mm});
            skLineSegment(sketch, "E321", {"start": v(-74.8, -31.6) * mm, "end": v(-72.84, -31.19) * mm});
            skLineSegment(sketch, "E322", {"start": v(-70.65, 35.3) * mm, "end": v(-71.45, -26.01) * mm});
            skLineSegment(sketch, "E323", {"start": v(-88.95, 35.3) * mm, "end": v(-88.14, -25.99) * mm});
            skLineSegment(sketch, "E324", {"start": v(-90.65, 63.6) * mm, "end": v(-90.38, 48.02) * mm});
            skArc(sketch, "E325", {"start": v(-90.65, 65.6) * mm, "mid": v(-90.74, 65.8) * mm, "end": v(-90.95, 65.9) * mm});
            skLineSegment(sketch, "E326", {"start": v(-90.95, 65.9) * mm, "end": v(-91.86, 65.9) * mm});
            skLineSegment(sketch, "E327", {"start": v(-90.65, 65.6) * mm, "end": v(-90.65, 63.62) * mm});
            skLineSegment(sketch, "E328", {"start": v(-89.03, 42.66) * mm, "end": v(-88.95, 35.3) * mm});
            skLineSegment(sketch, "E329", {"start": v(-68.94, 63.6) * mm, "end": v(-69.21, 48.02) * mm});
            skArc(sketch, "E330", {"start": v(-68.64, 65.9) * mm, "mid": v(-68.85, 65.8) * mm, "end": v(-68.94, 65.6) * mm});
            skLineSegment(sketch, "E331", {"start": v(-68.94, 65.6) * mm, "end": v(-68.94, 63.6) * mm});
            skLineSegment(sketch, "E332", {"start": v(-67.74, 65.9) * mm, "end": v(-68.64, 65.9) * mm});
            skLineSegment(sketch, "E333", {"start": v(-70.56, 42.66) * mm, "end": v(-70.65, 35.3) * mm});
            skLineSegment(sketch, "E334", {"start": v(-83.8, -30.1) * mm, "end": v(-86.01, -29.16) * mm});
            skArc(sketch, "E335", {"start": v(-88.14, -25.99) * mm, "mid": v(-87.55, -27.9) * mm, "end": v(-86.01, -29.16) * mm});
            skLineSegment(sketch, "E336", {"start": v(-75.8, -30.1) * mm, "end": v(-73.58, -29.16) * mm});
            skLineSegment(sketch, "E337", {"start": v(-75.8, -30.1) * mm, "end": v(-79.8, -30.1) * mm});
            skLineSegment(sketch, "E338", {"start": v(-83.8, -30.1) * mm, "end": v(-79.8, -30.1) * mm});
            skArc(sketch, "E339", {"start": v(-73.58, -29.16) * mm, "mid": v(-72.05, -27.9) * mm, "end": v(-71.45, -25.99) * mm});
            skArc(sketch, "E340", {"start": v(-91.86, 65.9) * mm, "mid": v(-92.04, 65.82) * mm, "end": v(-92.1, 65.65) * mm});
            skArc(sketch, "E341", {"start": v(-67.49, 65.65) * mm, "mid": v(-67.56, 65.82) * mm, "end": v(-67.74, 65.9) * mm});
            skLineSegment(sketch, "E342", {"start": v(-80.8, -36.6) * mm, "end": v(-78.8, -36.6) * mm});
            skArc(sketch, "E343", {"start": v(-90.38, 48.02) * mm, "mid": v(-90.2, 46.65) * mm, "end": v(-89.7, 45.36) * mm});
            skArc(sketch, "E344", {"start": v(-89.03, 42.66) * mm, "mid": v(-89.21, 44.05) * mm, "end": v(-89.7, 45.36) * mm});
            skArc(sketch, "E345", {"start": v(-69.89, 45.36) * mm, "mid": v(-69.4, 46.65) * mm, "end": v(-69.21, 48.02) * mm});
            skArc(sketch, "E346", {"start": v(-69.89, 45.36) * mm, "mid": v(-70.38, 44.05) * mm, "end": v(-70.56, 42.66) * mm});
            skSolve(sketch);
        }
        {
            var Q0;
            Q0=qCreatedBy(makeId("Front.planeOp"),FACE);
            var sketch = newSketch(context, id + "F1", { "sketchPlane" : qUnion([Q0])});
            skLineSegment(sketch, "E347.0", {"start": v(-90.39, 48.42) * mm, "end": v(-90.38, 48.02) * mm});
            skArc(sketch, "E348.0", {"start": v(-90.38, 48.02) * mm, "mid": v(-90.2, 46.65) * mm, "end": v(-89.7, 45.36) * mm});
            skArc(sketch, "E349.0", {"start": v(-89.03, 42.66) * mm, "mid": v(-89.21, 44.05) * mm, "end": v(-89.7, 45.36) * mm});
            skLineSegment(sketch, "E350.0", {"start": v(-89.03, 42.66) * mm, "end": v(-88.95, 35.3) * mm});
            skLineSegment(sketch, "E351.0", {"start": v(-88.95, 35.3) * mm, "end": v(-88.14, -25.99) * mm});
            skLineSegment(sketch, "E352.0", {"start": v(-91.55, 35.3) * mm, "end": v(-90.75, -25.6) * mm});
            skLineSegment(sketch, "E353.0", {"start": v(-91.8, 45.3) * mm, "end": v(-91.55, 35.3) * mm});
            skLineSegment(sketch, "E354.0", {"start": v(-91.85, 48.4) * mm, "end": v(-91.8, 45.3) * mm});
            skLineSegment(sketch, "E355.0", {"start": v(-83.8, -30.1) * mm, "end": v(-79.8, -30.1) * mm});
            skLineSegment(sketch, "E356.0", {"start": v(-80.8, -36.6) * mm, "end": v(-81.53, -32.43) * mm});
            skArc(sketch, "E357.0", {"start": v(-81.53, -32.43) * mm, "mid": v(-81.88, -31.84) * mm, "end": v(-82.52, -31.6) * mm});
            skLineSegment(sketch, "E358.0", {"start": v(-84.8, -31.6) * mm, "end": v(-82.52, -31.6) * mm});
            skLineSegment(sketch, "E359.0", {"start": v(-83.8, -30.1) * mm, "end": v(-86.01, -29.16) * mm});
            skLineSegment(sketch, "E360.0", {"start": v(-84.8, -31.6) * mm, "end": v(-86.75, -31.19) * mm});
            skArc(sketch, "E361.0", {"start": v(-90.71, -26.36) * mm, "mid": v(-89.58, -29.47) * mm, "end": v(-86.75, -31.19) * mm});
            skArc(sketch, "E362.0", {"start": v(-88.14, -25.99) * mm, "mid": v(-87.55, -27.9) * mm, "end": v(-86.01, -29.16) * mm});
            skLineSegment(sketch, "E363.0", {"start": v(-90.72, -25.6) * mm, "end": v(-90.71, -26.36) * mm});
            skLineSegment(sketch, "E364", {"start": v(-90.72, -25.6) * mm, "end": v(-90.75, -25.6) * mm});
            skLineSegment(sketch, "E365", {"start": v(-79.8, -30.1) * mm, "end": v(-79.8, -36.6) * mm});
            skLineSegment(sketch, "E366.0", {"start": v(-80.8, -36.6) * mm, "end": v(-79.8, -36.6) * mm});
            skPoint(sketch, "E367.orphan", {"position": v(-78.8, -36.6) * mm});
            skLineSegment(sketch, "E368", {"start": v(-91.85, 48.4) * mm, "end": v(-90.39, 48.42) * mm});
            skSolve(sketch);
        }
        {
            var Q0;
            Q0=makeQuery(id+"F1.imprint","IMPRINT",FACE,{"disambiguationData":[TD([[makeQuery(id+"F1.imprint","IMPRINT",EDGE,{"derivedFrom":sQuery(id+"F1.wireOp",EDGE,"E347.0")}),-1.0]])]});
            var Q1;
            Q1=sQuery(id+"F1.wireOp",EDGE,"E365");
            revolve(context, id + "F2", {"entities" : qUnion([Q0]), "axis" : qUnion([Q1]), "revolveType" : RevolveType.FULL});
        }
        {
            var Q0;
            Q0=qCreatedBy(makeId("Front.planeOp"),FACE);
            var sketch = newSketch(context, id + "F3", { "sketchPlane" : qUnion([Q0])});
            skLineSegment(sketch, "E369.0", {"start": v(-90.65, 63.6) * mm, "end": v(-90.39, 48.4) * mm});
            skLineSegment(sketch, "E370.0", {"start": v(-91.85, 48.4) * mm, "end": v(-91.85, 49.68) * mm});
            skArc(sketch, "E371.0", {"start": v(-91.85, 49.68) * mm, "mid": v(-92, 50.12) * mm, "end": v(-92.38, 50.36) * mm});
            skLineSegment(sketch, "E372.0", {"start": v(-92.38, 50.36) * mm, "end": v(-93.42, 50.62) * mm});
            skArc(sketch, "E373.0", {"start": v(-93.68, 51) * mm, "mid": v(-93.62, 50.76) * mm, "end": v(-93.42, 50.62) * mm});
            skLineSegment(sketch, "E374.0", {"start": v(-93.3, 54.02) * mm, "end": v(-93.68, 51) * mm});
            skArc(sketch, "E375.0", {"start": v(-92.3, 54.9) * mm, "mid": v(-92.97, 54.65) * mm, "end": v(-93.3, 54.02) * mm});
            skArc(sketch, "E376.0", {"start": v(-92.3, 54.9) * mm, "mid": v(-92.17, 54.95) * mm, "end": v(-92.1, 55.1) * mm});
            skLineSegment(sketch, "E377.0", {"start": v(-92.1, 56.09) * mm, "end": v(-92.1, 55.1) * mm});
            skArc(sketch, "E378.0", {"start": v(-92.1, 56.09) * mm, "mid": v(-92.14, 56.2) * mm, "end": v(-92.24, 56.28) * mm});
            skLineSegment(sketch, "E379.0", {"start": v(-92.24, 56.28) * mm, "end": v(-92.96, 56.54) * mm});
            skArc(sketch, "E380.0", {"start": v(-92.96, 57.99) * mm, "mid": v(-93.47, 57.26) * mm, "end": v(-92.96, 56.54) * mm});
            skLineSegment(sketch, "E381.0", {"start": v(-92.24, 58.25) * mm, "end": v(-92.96, 57.99) * mm});
            skArc(sketch, "E382.0", {"start": v(-92.24, 58.25) * mm, "mid": v(-92.14, 58.32) * mm, "end": v(-92.1, 58.44) * mm});
            skLineSegment(sketch, "E383.0", {"start": v(-92.1, 59.69) * mm, "end": v(-92.1, 58.44) * mm});
            skArc(sketch, "E384.0", {"start": v(-92.1, 59.69) * mm, "mid": v(-92.14, 59.8) * mm, "end": v(-92.24, 59.88) * mm});
            skLineSegment(sketch, "E385.0", {"start": v(-92.24, 59.88) * mm, "end": v(-92.96, 60.14) * mm});
            skArc(sketch, "E386.0", {"start": v(-92.96, 61.59) * mm, "mid": v(-93.47, 60.86) * mm, "end": v(-92.96, 60.14) * mm});
            skPoint(sketch, "E387.0", {"position": v(-92.6, 61.72) * mm});
            skLineSegment(sketch, "E388.0", {"start": v(-92.24, 61.85) * mm, "end": v(-92.96, 61.59) * mm});
            skPoint(sketch, "E389.0", {"position": v(-92.14, 61.92) * mm});
            skLineSegment(sketch, "E390.0", {"start": v(-92.1, 62.9) * mm, "end": v(-92.1, 62.04) * mm});
            skArc(sketch, "E391.0", {"start": v(-92.24, 61.85) * mm, "mid": v(-92.14, 61.92) * mm, "end": v(-92.1, 62.04) * mm});
            skLineSegment(sketch, "E392.0", {"start": v(-92.1, 65.65) * mm, "end": v(-92.1, 62.9) * mm});
            skArc(sketch, "E393.0", {"start": v(-91.86, 65.9) * mm, "mid": v(-92.04, 65.82) * mm, "end": v(-92.1, 65.65) * mm});
            skLineSegment(sketch, "E394.0", {"start": v(-90.95, 65.9) * mm, "end": v(-91.86, 65.9) * mm});
            skArc(sketch, "E395.0", {"start": v(-90.65, 65.6) * mm, "mid": v(-90.74, 65.8) * mm, "end": v(-90.95, 65.9) * mm});
            skLineSegment(sketch, "E396.0", {"start": v(-90.65, 65.6) * mm, "end": v(-90.65, 63.62) * mm});
            skLineSegment(sketch, "E397", {"start": v(-90.65, 63.62) * mm, "end": v(-90.65, 63.6) * mm});
            skLineSegment(sketch, "E398", {"start": v(-91.85, 48.4) * mm, "end": v(-90.39, 48.4) * mm});
            skPoint(sketch, "E399.orphan", {"position": v(-90.38, 48.02) * mm});
            skPoint(sketch, "E400.0", {"position": v(-79.8, -30.1) * mm});
            skPoint(sketch, "E401.0", {"position": v(-79.8, -36.6) * mm});
            skLineSegment(sketch, "E402", {"start": v(-79.8, -36.6) * mm, "end": v(-79.8, -12.86) * mm});
            skSolve(sketch);
        }
        {
            var Q0;
            Q0=makeQuery(id+"F3.imprint","IMPRINT",FACE,{"disambiguationData":[TD([[makeQuery(id+"F3.imprint","IMPRINT",EDGE,{"derivedFrom":sQuery(id+"F3.wireOp",EDGE,"E369.0")}),-1.0]])]});
            var Q1;
            Q1=sQuery(id+"F3.wireOp",EDGE,"E402");
            revolve(context, id + "F4", {"entities" : qUnion([Q0]), "axis" : qUnion([Q1]), "revolveType" : RevolveType.FULL});
        }
        {
            var Q0;
            Q0=qCreatedBy(makeId("Front.planeOp"),FACE);
            var sketch = newSketch(context, id + "F5", { "sketchPlane" : qUnion([Q0])});
            skLineSegment(sketch, "E403.0", {"start": v(-41.8, 45.3) * mm, "end": v(-41.55, 35.3) * mm});
            skArc(sketch, "E404.0", {"start": v(-38.53, 41.67) * mm, "mid": v(-38.76, 43.24) * mm, "end": v(-39.39, 44.69) * mm});
            skLineSegment(sketch, "E405.0", {"start": v(-39.53, 44.92) * mm, "end": v(-39.39, 44.69) * mm});
            skArc(sketch, "E406.0", {"start": v(-40.38, 47.9) * mm, "mid": v(-40.15, 46.35) * mm, "end": v(-39.53, 44.92) * mm});
            skLineSegment(sketch, "E407.0", {"start": v(-38.53, 41.67) * mm, "end": v(-38.46, 35.3) * mm});
            skLineSegment(sketch, "E408.0", {"start": v(-38.46, 35.3) * mm, "end": v(-37.65, -26.1) * mm});
            skLineSegment(sketch, "E409.0", {"start": v(-41.55, 35.3) * mm, "end": v(-40.75, -25.6) * mm});
            skArc(sketch, "E410.0", {"start": v(-37.65, -26.1) * mm, "mid": v(-37.06, -28) * mm, "end": v(-35.52, -29.27) * mm});
            skLineSegment(sketch, "E411.0", {"start": v(-33.8, -30) * mm, "end": v(-35.52, -29.27) * mm});
            skLineSegment(sketch, "E412.0", {"start": v(-33.8, -30) * mm, "end": v(-29.8, -30) * mm});
            skLineSegment(sketch, "E413.0", {"start": v(-30.6, -36.6) * mm, "end": v(-31.33, -32.43) * mm});
            skArc(sketch, "E414.0", {"start": v(-31.33, -32.43) * mm, "mid": v(-31.68, -31.84) * mm, "end": v(-32.32, -31.6) * mm});
            skLineSegment(sketch, "E415.0", {"start": v(-30.6, -36.6) * mm, "end": v(-29.8, -36.6) * mm});
            skLineSegment(sketch, "E416.0", {"start": v(-34.8, -31.6) * mm, "end": v(-32.32, -31.6) * mm});
            skLineSegment(sketch, "E417.0", {"start": v(-34.8, -31.6) * mm, "end": v(-37.66, -30.5) * mm});
            skLineSegment(sketch, "E418.0", {"start": v(-40.75, -25.6) * mm, "end": v(-40.74, -26.09) * mm});
            skArc(sketch, "E419.0", {"start": v(-40.74, -26.09) * mm, "mid": v(-39.88, -28.77) * mm, "end": v(-37.66, -30.5) * mm});
            skLineSegment(sketch, "E420.0", {"start": v(-41.85, 48.4) * mm, "end": v(-41.8, 45.3) * mm});
            skLineSegment(sketch, "E421.0", {"start": v(-40.39, 48.4) * mm, "end": v(-40.38, 47.9) * mm});
            skLineSegment(sketch, "E422", {"start": v(-41.85, 48.4) * mm, "end": v(-40.39, 48.4) * mm});
            skPoint(sketch, "E423.orphan", {"position": v(-40.65, 63.6) * mm});
            skLineSegment(sketch, "E424", {"start": v(-29.8, -36.6) * mm, "end": v(-29.8, 12.55) * mm});
            skSolve(sketch);
        }
        {
            var Q0;
            Q0=makeQuery(id+"F5.imprint","IMPRINT",FACE,{"disambiguationData":[TD([[makeQuery(id+"F5.imprint","IMPRINT",EDGE,{"derivedFrom":sQuery(id+"F5.wireOp",EDGE,"E403.0")}),1.0]])]});
            var Q1;
            Q1=sQuery(id+"F5.wireOp",EDGE,"E424");
            revolve(context, id + "F6", {"entities" : qUnion([Q0]), "axis" : qUnion([Q1]), "revolveType" : RevolveType.FULL});
        }
        {
            var Q0;
            Q0=qCreatedBy(makeId("Front.planeOp"),FACE);
            var sketch = newSketch(context, id + "F7", { "sketchPlane" : qUnion([Q0])});
            skLineSegment(sketch, "E425.0", {"start": v(8.15, 48.4) * mm, "end": v(8.2, 45.3) * mm});
            skArc(sketch, "E426.0", {"start": v(9.61, 48.24) * mm, "mid": v(9.93, 46.43) * mm, "end": v(10.77, 44.8) * mm});
            skArc(sketch, "E427.0", {"start": v(11.92, 41.34) * mm, "mid": v(11.61, 43.16) * mm, "end": v(10.77, 44.8) * mm});
            skLineSegment(sketch, "E428.0", {"start": v(9.61, 48.42) * mm, "end": v(9.61, 48.24) * mm});
            skLineSegment(sketch, "E429.0", {"start": v(11.92, 41.34) * mm, "end": v(12, 35.3) * mm});
            skLineSegment(sketch, "E430.0", {"start": v(8.2, 45.3) * mm, "end": v(8.45, 35.3) * mm});
            skLineSegment(sketch, "E431.0", {"start": v(8.45, 35.3) * mm, "end": v(9.25, -25.6) * mm});
            skLineSegment(sketch, "E432.0", {"start": v(12, 35.3) * mm, "end": v(12.8, -26.29) * mm});
            skArc(sketch, "E433.0", {"start": v(12.8, -26.29) * mm, "mid": v(13.4, -28.2) * mm, "end": v(14.93, -29.46) * mm});
            skLineSegment(sketch, "E434.0", {"start": v(16.2, -30) * mm, "end": v(14.93, -29.46) * mm});
            skLineSegment(sketch, "E435.0", {"start": v(16.2, -30) * mm, "end": v(20.2, -30) * mm});
            skLineSegment(sketch, "E436.0", {"start": v(9.28, -25.6) * mm, "end": v(9.29, -26.36) * mm});
            skArc(sketch, "E437.0", {"start": v(9.29, -26.36) * mm, "mid": v(10.42, -29.47) * mm, "end": v(13.25, -31.19) * mm});
            skLineSegment(sketch, "E438.0", {"start": v(15.2, -31.6) * mm, "end": v(13.25, -31.19) * mm});
            skLineSegment(sketch, "E439.0", {"start": v(15.2, -31.6) * mm, "end": v(17.48, -31.6) * mm});
            skArc(sketch, "E440.0", {"start": v(18.47, -32.43) * mm, "mid": v(18.12, -31.84) * mm, "end": v(17.48, -31.6) * mm});
            skLineSegment(sketch, "E441.0", {"start": v(19.2, -36.6) * mm, "end": v(18.47, -32.43) * mm});
            skLineSegment(sketch, "E442.0", {"start": v(19.2, -36.6) * mm, "end": v(20.2, -36.6) * mm});
            skLineSegment(sketch, "E443", {"start": v(9.28, -25.6) * mm, "end": v(9.25, -25.6) * mm});
            skLineSegment(sketch, "E444", {"start": v(20.2, -30) * mm, "end": v(20.2, -36.6) * mm});
            skPoint(sketch, "E445.orphan", {"position": v(21.2, -36.6) * mm});
            skLineSegment(sketch, "E446", {"start": v(8.15, 48.4) * mm, "end": v(9.61, 48.42) * mm});
            skPoint(sketch, "E447.orphan", {"position": v(9.35, 63.6) * mm});
            skSolve(sketch);
        }
        {
            var Q0;
            Q0=makeQuery(id+"F7.imprint","IMPRINT",FACE,{"disambiguationData":[TD([[makeQuery(id+"F7.imprint","IMPRINT",EDGE,{"derivedFrom":sQuery(id+"F7.wireOp",EDGE,"E425.0")}),1.0]])]});
            var Q1;
            Q1=sQuery(id+"F7.wireOp",EDGE,"E444");
            revolve(context, id + "F8", {"entities" : qUnion([Q0]), "axis" : qUnion([Q1]), "revolveType" : RevolveType.FULL});
        }
        {
            var Q0;
            Q0=qCreatedBy(makeId("Front.planeOp"),FACE);
            var sketch = newSketch(context, id + "F9", { "sketchPlane" : qUnion([Q0])});
            skLineSegment(sketch, "E448.0", {"start": v(57.45, 48.4) * mm, "end": v(57.48, 45.4) * mm});
            skLineSegment(sketch, "E449.0", {"start": v(59.64, 48.4) * mm, "end": v(57.45, 48.4) * mm});
            skLineSegment(sketch, "E450.0", {"start": v(59.64, 48.4) * mm, "end": v(59.67, 46.79) * mm});
            skArc(sketch, "E451.0", {"start": v(59.67, 46.79) * mm, "mid": v(59.7, 46.4) * mm, "end": v(59.78, 46.02) * mm});
            skLineSegment(sketch, "E452.0", {"start": v(59.78, 46.02) * mm, "end": v(60.42, 43.78) * mm});
            skArc(sketch, "E453.0", {"start": v(60.54, 43) * mm, "mid": v(60.5, 43.4) * mm, "end": v(60.42, 43.78) * mm});
            skLineSegment(sketch, "E454.0", {"start": v(60.54, 43) * mm, "end": v(60.64, 34.4) * mm});
            skLineSegment(sketch, "E455.0", {"start": v(57.48, 45.4) * mm, "end": v(57.65, 35.4) * mm});
            skLineSegment(sketch, "E456.0", {"start": v(57.65, 35.4) * mm, "end": v(58.96, -64.6) * mm});
            skLineSegment(sketch, "E457.0", {"start": v(61.67, -40.1) * mm, "end": v(60.64, 34.4) * mm});
            skLineSegment(sketch, "E458.0", {"start": v(62.3, -65.44) * mm, "end": v(61.67, -40.1) * mm});
            skLineSegment(sketch, "E459.0", {"start": v(58.96, -64.6) * mm, "end": v(58.97, -65.37) * mm});
            skArc(sketch, "E460.0", {"start": v(58.97, -65.37) * mm, "mid": v(60.3, -69.03) * mm, "end": v(63.64, -71.06) * mm});
            skArc(sketch, "E461.0", {"start": v(62.3, -65.44) * mm, "mid": v(63.25, -68.12) * mm, "end": v(65.63, -69.68) * mm});
            skLineSegment(sketch, "E462.0", {"start": v(70.2, -70.1) * mm, "end": v(67.2, -70.1) * mm});
            skLineSegment(sketch, "E463.0", {"start": v(67.2, -70.1) * mm, "end": v(65.63, -69.68) * mm});
            skLineSegment(sketch, "E464.0", {"start": v(66.2, -71.6) * mm, "end": v(67.48, -71.6) * mm});
            skLineSegment(sketch, "E465.0", {"start": v(66.2, -71.6) * mm, "end": v(63.57, -71.04) * mm});
            skArc(sketch, "E466.0", {"start": v(68.47, -72.43) * mm, "mid": v(68.12, -71.84) * mm, "end": v(67.48, -71.6) * mm});
            skLineSegment(sketch, "E467.0", {"start": v(69.2, -76.6) * mm, "end": v(68.47, -72.43) * mm});
            skLineSegment(sketch, "E468.0", {"start": v(70.2, -76.6) * mm, "end": v(69.2, -76.6) * mm});
            skLineSegment(sketch, "E469", {"start": v(70.2, -70.1) * mm, "end": v(70.2, -76.6) * mm});
            skPoint(sketch, "E470.orphan", {"position": v(71.2, -76.6) * mm});
            skPoint(sketch, "E471.orphan", {"position": v(58.32, 48.4) * mm});
            skPoint(sketch, "E472.orphan", {"position": v(59.37, 63.6) * mm});
            skSolve(sketch);
        }
        {
            var Q0;
            Q0 = qSketchRegion(id + "F9", true);
            var Q1;
            Q1=sQuery(id+"F9.wireOp",EDGE,"E469");
            revolve(context, id + "F10", {"entities" : qUnion([Q0]), "axis" : qUnion([Q1]), "revolveType" : RevolveType.FULL});
        }
    });
